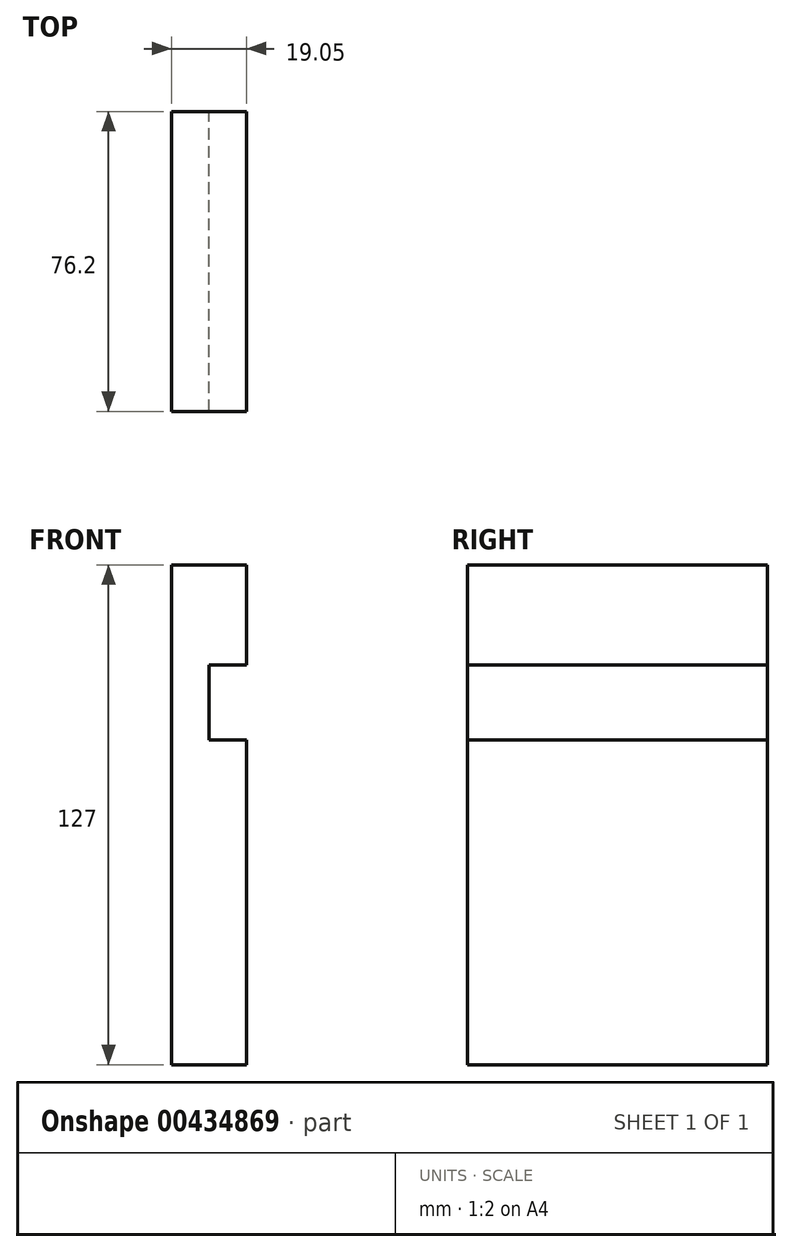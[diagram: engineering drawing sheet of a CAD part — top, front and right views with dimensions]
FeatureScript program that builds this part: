
annotation { "Feature Type Name" : "Feature", "Feature Type Description" : "" }
export const myFeature = defineFeature(function(context is Context, id is Id, definition is map)
    precondition{}
    {
        {
            var Q0;
            Q0=qCreatedBy(makeId("Front.planeOp"),FACE);
            var sketch = newSketch(context, id + "F0", { "sketchPlane" : qUnion([Q0])});
            skLineSegment(sketch, "E0", {"start": v(0, 0) * mm, "end": v(0, 127) * mm});
            skLineSegment(sketch, "E1", {"start": v(0, 127) * mm, "end": v(19.05, 127) * mm});
            skLineSegment(sketch, "E2", {"start": v(19.05, 127) * mm, "end": v(19.05, 101.6) * mm});
            skLineSegment(sketch, "E3", {"start": v(19.05, 101.6) * mm, "end": v(9.53, 101.6) * mm});
            skLineSegment(sketch, "E4", {"start": v(9.53, 101.6) * mm, "end": v(9.53, 82.55) * mm});
            skLineSegment(sketch, "E5", {"start": v(9.53, 82.55) * mm, "end": v(19.05, 82.55) * mm});
            skLineSegment(sketch, "E6", {"start": v(19.05, 82.55) * mm, "end": v(19.05, 0) * mm});
            skLineSegment(sketch, "E7", {"start": v(19.05, 0) * mm, "end": v(0, 0) * mm});
            skSolve(sketch);
        }
        {
            var Q0;
            Q0 = qSketchRegion(id + "F0", true);
            extrude(context, id + "F1", {"entities" : qUnion([Q0]), "depth" : 76.2 * mm});
        }
    });
